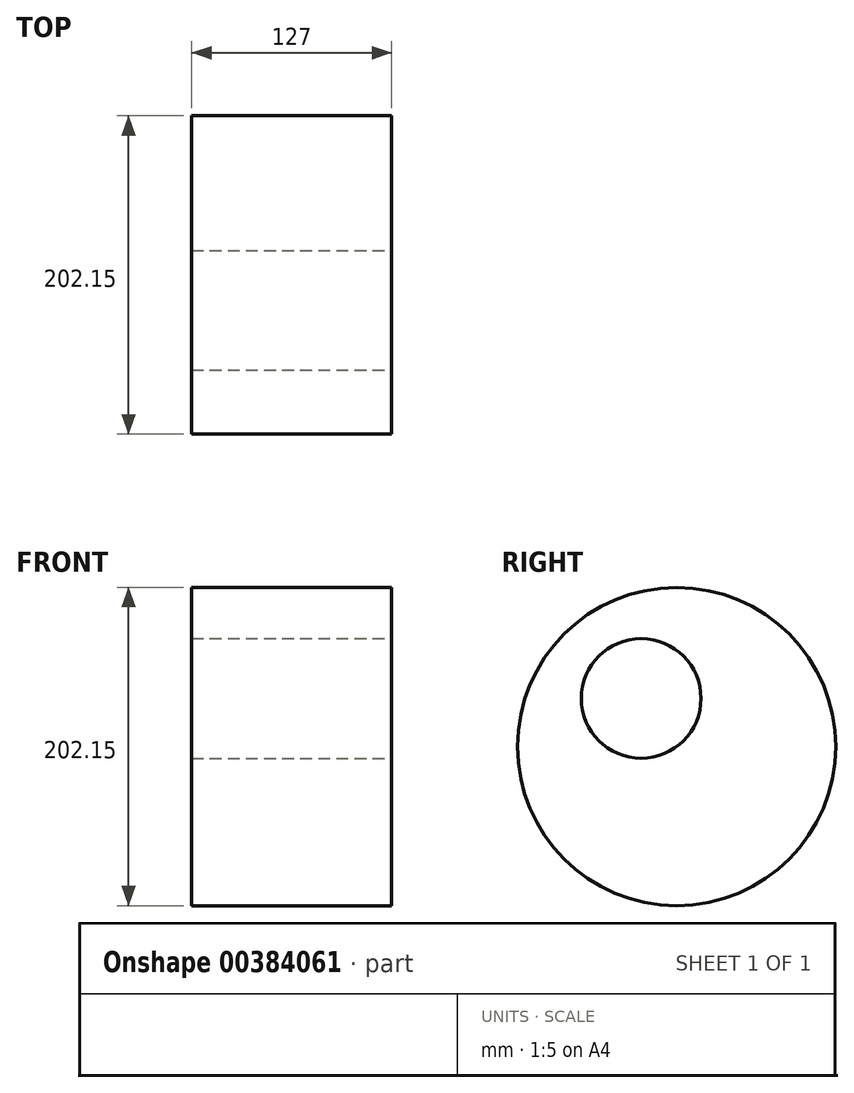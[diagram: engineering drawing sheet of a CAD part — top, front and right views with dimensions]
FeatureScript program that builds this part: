
annotation { "Feature Type Name" : "Feature", "Feature Type Description" : "" }
export const myFeature = defineFeature(function(context is Context, id is Id, definition is map)
    precondition{}
    {
        {
            var Q0;
            Q0=qCreatedBy(makeId("Right.planeOp"),FACE);
            var sketch = newSketch(context, id + "F0", { "sketchPlane" : qUnion([Q0])});
            skCircle(sketch, "E0", {"center": v(-42.47, 51.88) * mm, "radius": 38 * mm});
            skCircle(sketch, "E1", {"center": v(-19.9, 21.3) * mm, "radius": 101.07 * mm});
            skCircle(sketch, "E2", {"center": v(67.4, -63.28) * mm, "radius": 21.15 * mm});
            skSolve(sketch);
        }
        {
            var Q0;
            Q0=sQuery(id+"F0.wireOp",EDGE,"E0");
            var Q1;
            Q1=sQuery(id+"F0.wireOp",EDGE,"E1");
            extrude(context, id + "F1", {"bodyType" : ToolBodyType.SURFACE, "surfaceEntities" : qUnion([Q0, Q1]), "depth" : 127 * mm});
        }
    });
